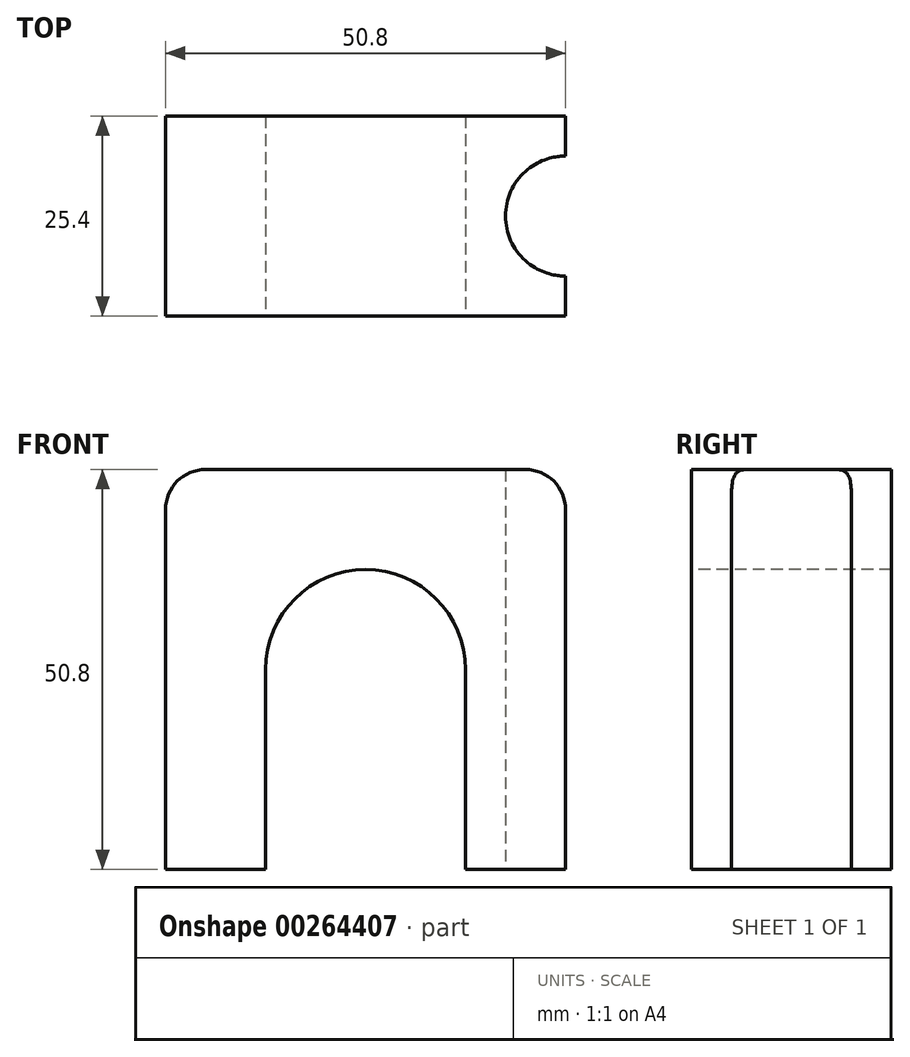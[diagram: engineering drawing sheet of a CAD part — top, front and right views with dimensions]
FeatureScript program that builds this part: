
annotation { "Feature Type Name" : "Feature", "Feature Type Description" : "" }
export const myFeature = defineFeature(function(context is Context, id is Id, definition is map)
    precondition{}
    {
        {
            var Q0;
            Q0=qCreatedBy(makeId("Top.planeOp"),FACE);
            var sketch = newSketch(context, id + "F0", { "sketchPlane" : qUnion([Q0])});
            skLineSegment(sketch, "E0.bottom", {"start": v(0, 0) * mm, "end": v(50.8, 0) * mm});
            skLineSegment(sketch, "E0.top", {"start": v(0, 25.4) * mm, "end": v(50.8, 25.4) * mm});
            skLineSegment(sketch, "E0.left", {"start": v(0, 0) * mm, "end": v(0, 25.4) * mm});
            skLineSegment(sketch, "E0.right", {"start": v(50.8, 0) * mm, "end": v(50.8, 25.4) * mm});
            skCircle(sketch, "E1", {"center": v(50.8, 12.7) * mm, "radius": 7.62 * mm});
            skSolve(sketch);
        }
        {
            var Q0;
            Q0=makeQuery(id+"F0.imprint","IMPRINT",FACE,{"disambiguationData":[TD([[makeQuery(id+"F0.imprint","IMPRINT",EDGE,{"derivedFrom":sQuery(id+"F0.wireOp",EDGE,"E0.bottom")}),1.0]])]});
            var Q1;
            {var subQ0=sQuery(id+"F0.wireOp",EDGE,"E1");var subQ1=sQuery(id+"F0.wireOp",EDGE,"E0.right");var subQ2=makeQuery(id+"F0.imprint","INTERSECT",VERTEX,{"disambiguationData":[OD(0.0)],"derivedFrom":[subQ1,subQ0]});Q1=makeQuery(id+"F0.imprint","IMPRINT",FACE,{"disambiguationData":[TD([[makeQuery(id+"F0.imprint","IMPRINT",EDGE,{"disambiguationData":[TD([[subQ2,-1.0]])],"derivedFrom":subQ1}),-1.0]])]});}
            var Q2;
            {var subQ0=sQuery(id+"F0.wireOp",EDGE,"E1");var subQ1=sQuery(id+"F0.wireOp",EDGE,"E0.right");var subQ2=makeQuery(id+"F0.imprint","INTERSECT",VERTEX,{"disambiguationData":[OD(0.0)],"derivedFrom":[subQ1,subQ0]});Q2=makeQuery(id+"F0.imprint","IMPRINT",FACE,{"disambiguationData":[TD([[makeQuery(id+"F0.imprint","IMPRINT",EDGE,{"disambiguationData":[TD([[subQ2,-1.0]])],"derivedFrom":subQ1}),1.0]])]});}
            extrude(context, id + "F1", {"entities" : qUnion([Q0, Q1, Q2]), "depth" : 50.8 * mm});
        }
        {
            var Q0;
            Q0=makeQuery(id+"F1.opExtrude","SWEPT_FACE",FACE,{"disambiguationData":[OSD([sQuery(id+"F0.wireOp",EDGE,"E0.bottom")])]});
            var sketch = newSketch(context, id + "F2", { "sketchPlane" : qUnion([Q0])});
            skLineSegment(sketch, "E2.bottom", {"start": v(12.7, 0) * mm, "end": v(38.1, 0) * mm});
            skLineSegment(sketch, "E2.top", {"start": v(12.7, 25.4) * mm, "end": v(38.1, 25.4) * mm});
            skLineSegment(sketch, "E2.left", {"start": v(12.7, 0) * mm, "end": v(12.7, 25.4) * mm});
            skLineSegment(sketch, "E2.right", {"start": v(38.1, 0) * mm, "end": v(38.1, 25.4) * mm});
            skCircle(sketch, "E3", {"center": v(25.4, 25.4) * mm, "radius": 12.7 * mm});
            skSolve(sketch);
        }
        {
            var Q0;
            {var subQ0=sQuery(id+"F2.wireOp",EDGE,"E2.top");Q0=makeQuery(id+"F2.imprint","IMPRINT",FACE,{"disambiguationData":[TD([[makeQuery(id+"F2.imprint","IMPRINT",EDGE,{"derivedFrom":subQ0}),1.0]])]});}
            var Q1;
            {var subQ0=sQuery(id+"F2.wireOp",EDGE,"E2.top");Q1=makeQuery(id+"F2.imprint","IMPRINT",FACE,{"disambiguationData":[TD([[makeQuery(id+"F2.imprint","IMPRINT",EDGE,{"derivedFrom":subQ0}),-1.0]])]});}
            var Q2;
            Q2=makeQuery(id+"F2.imprint","IMPRINT",FACE,{"disambiguationData":[TD([[makeQuery(id+"F2.imprint","IMPRINT",EDGE,{"derivedFrom":sQuery(id+"F2.wireOp",EDGE,"E2.bottom")}),1.0]])]});
            extrude(context, id + "F3", {"entities" : qUnion([Q0, Q1, Q2]), "operationType" : NewBodyOperationType.REMOVE, "oppositeDirection" : true, "depth" : 25.4 * mm});
        }
        {
            var Q0;
            Q0=makeQuery(id+"F1.opExtrude","CAP_EDGE",EDGE,{"disambiguationData":[OSD([sQuery(id+"F0.wireOp",EDGE,"E0.left")])],"isStart":false});
            var Q1;
            Q1=makeQuery(id+"F1.opExtrude","CAP_EDGE",EDGE,{"disambiguationData":[OSD([sQuery(id+"F0.wireOp",EDGE,"E0.right")])],"isStart":false});
            fillet(context, id + "F4", {"entities" : qUnion([Q0, Q1]), "radius" : 5.08 * mm, "tangentPropagation" : true, "allowEdgeOverflow" : false});
        }
        {
            var Q0;
            Q0=makeQuery(id+"F1.opExtrude","CAP_FACE",FACE,{"disambiguationData":[OSD([sQuery(id+"F0.wireOp",EDGE,"E0.bottom"),sQuery(id+"F0.wireOp",EDGE,"E0.top"),sQuery(id+"F0.wireOp",EDGE,"E0.left"),sQuery(id+"F0.wireOp",EDGE,"E0.right"),sQuery(id+"F0.wireOp",EDGE,"E1")])],"isStart":false});
            var sketch = newSketch(context, id + "F5", { "sketchPlane" : qUnion([Q0])});
            skPoint(sketch, "E4", {"position": v(50.8, 12.7) * mm});
            skSolve(sketch);
        }
        {
            var Q0;
            Q0=sQuery(id+"F5.wireOp",VERTEX,"E4");
            var Q1;
            Q1=makeQuery(id+"F1.opExtrude","SWEPT_BODY",BODY,{"disambiguationData":[OSD([sQuery(id+"F0.wireOp",EDGE,"E0.bottom"),sQuery(id+"F0.wireOp",EDGE,"E0.top"),sQuery(id+"F0.wireOp",EDGE,"E0.left"),sQuery(id+"F0.wireOp",EDGE,"E0.right"),sQuery(id+"F0.wireOp",EDGE,"E1")])]});
            hole(context, id + "F6", {"style" : HoleStyle.SIMPLE, "endStyle" : HoleEndStyle.THROUGH, "holeDiameter" : 7.62 * mm, "tappedDepth" : 12.7 * mm, "tapClearance" : 3, "locations" : qUnion([Q0]), "scope" : qUnion([Q1])});
        }
    });
